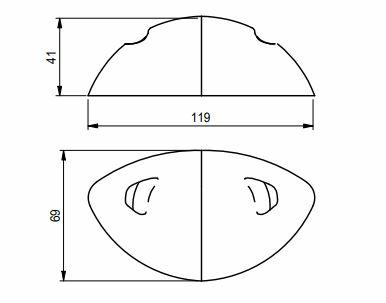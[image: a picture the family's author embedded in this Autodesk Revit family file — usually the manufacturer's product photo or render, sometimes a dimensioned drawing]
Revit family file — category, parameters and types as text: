
# Revit family: R-MBD-491
name_source: partatom
category: Portes
units: mm (PartAtom-declared; Revit-internal decimal feet)

## family parameters
Couper avec des vides une fois chargée = Non
Hôte = Mur
Partagée = Non
Repère de localisation dans la pièce = Oui
Toujours verticalement = Oui

## types (1)
- MBD-491
    1 Vantail = Oui
    2 Vantaux = Non
    A.E.V = non
    Acoustique = non
    Anti-Effraction = non
    Certification = D.A.S. Mode 2 certifié NF
    Code_MAJ = 2303130305MBD491
    Coloris_Chants = BER
    Coloris_Dormant = Hêtre
    Coloris_Face_Cote_Oppose_Ouverture = Prépeint
    Coloris_Face_Cote_Ouverture = Prépeint
    Construction analytique = <Aucun>
    DAS = Oui
    DC Larg Feuillure = 12 mm  [stored 0.0393701 ft]
    DC Pivot Vantail = 60 mm  [stored 0.19685 ft]
    Description = Bloc-porte bois D.A.S. 1 vantail SP51 avec pivot linteau motorisé encastré, double action / va-et-vient, EI60, D.A.S. certifié NF, sur huisserie bois sans montant sans fileur
    Définir les propriétés thermiques par = Type schématique
    Ep Profil Pose Tunnel = 118 mm
    Ep Strat Vantail = 1 mm  [stored 0.00328084 ft]
    Ep Vantail = 46 mm  [stored 0.150919 ft]
    Epaisseur_Rainure à brique = 8 mm  [stored 0.0262467 ft]
    Fabricant = MALERBA
    Fiche_Produit = MBD-491
    Fileur = Non
    Hauteur_Tableau = 2125 mm
    Hauteur_Vantaux_Souhaitée = 2040 mm  [stored 6.69291 ft]
    Jeu_1 = 0 mm  [stored 0 ft]
    Jeu_2 = 0 mm  [stored 0 ft]
    Jeu_Côté_Articulation_Vantail = 8 mm  [stored 0.0262467 ft]
    Jeu_Côté_Fermeture_Vantail = 8 mm  [stored 0.0262467 ft]
    Jeu_Haut = 3 mm  [stored 0.00984252 ft]
    Larg Profil = 58 mm  [stored 0.190289 ft]
    Larg Profil Avec Fileur = 20 mm  [stored 0.0656168 ft]
    Larg Profil Trav = 76 mm  [stored 0.249344 ft]
    Largeur = 0 mm  [stored 0 ft]
    Largeur_Vantail_Semi_Fixe_Souhaitée = 930 mm  [stored 3.05118 ft]
    Largeur_Vantail_Service_Souhaitée = 930 mm  [stored 3.05118 ft]
    Mat APD = Caoutchouc noir
    Mat Parclose = BER 2
    Mat Parclose Métal = Peinture Laquée PMT - Blanc Pur - RAL 9010
    Materiaux_Dominant = Bois
    Modèle = Va et vient
    Montant_VV = Non
    Note d'identification = 1V EI60/SP51 DAS - LINTEAU MOTORISE - SANS MONTANT SANS FILEUR
    Pivot linteau motorisé = Oui
    Profondeur_Rainure à brique = 5 mm  [stored 0.0164042 ft]
    Reference_Commerciale = 1V SP51/DA LINTEAU OP
    Resistance_Feu = EI30
    Sans_Montants = Oui
    Sens_Feu = Recto / Verso
    Thermique (W/m2.°K) = 0
    URL = https://www.malerba.fr
    X_Axe Pivot = 68 mm  [stored 0.223097 ft]
    X_DC seuil = 9 mm  [stored 0.0295276 ft]
    X_Inv_DC Larg Feuillure_1V Montant = 0 mm  [stored 0 ft]

note: [stored X ft] marks values corroborated as IEEE doubles in the binary element streams (Revit-internal decimal feet)

## geometry (parser evidence)
native form markers: Blend x14
no freeform markers — native parametric forms only
